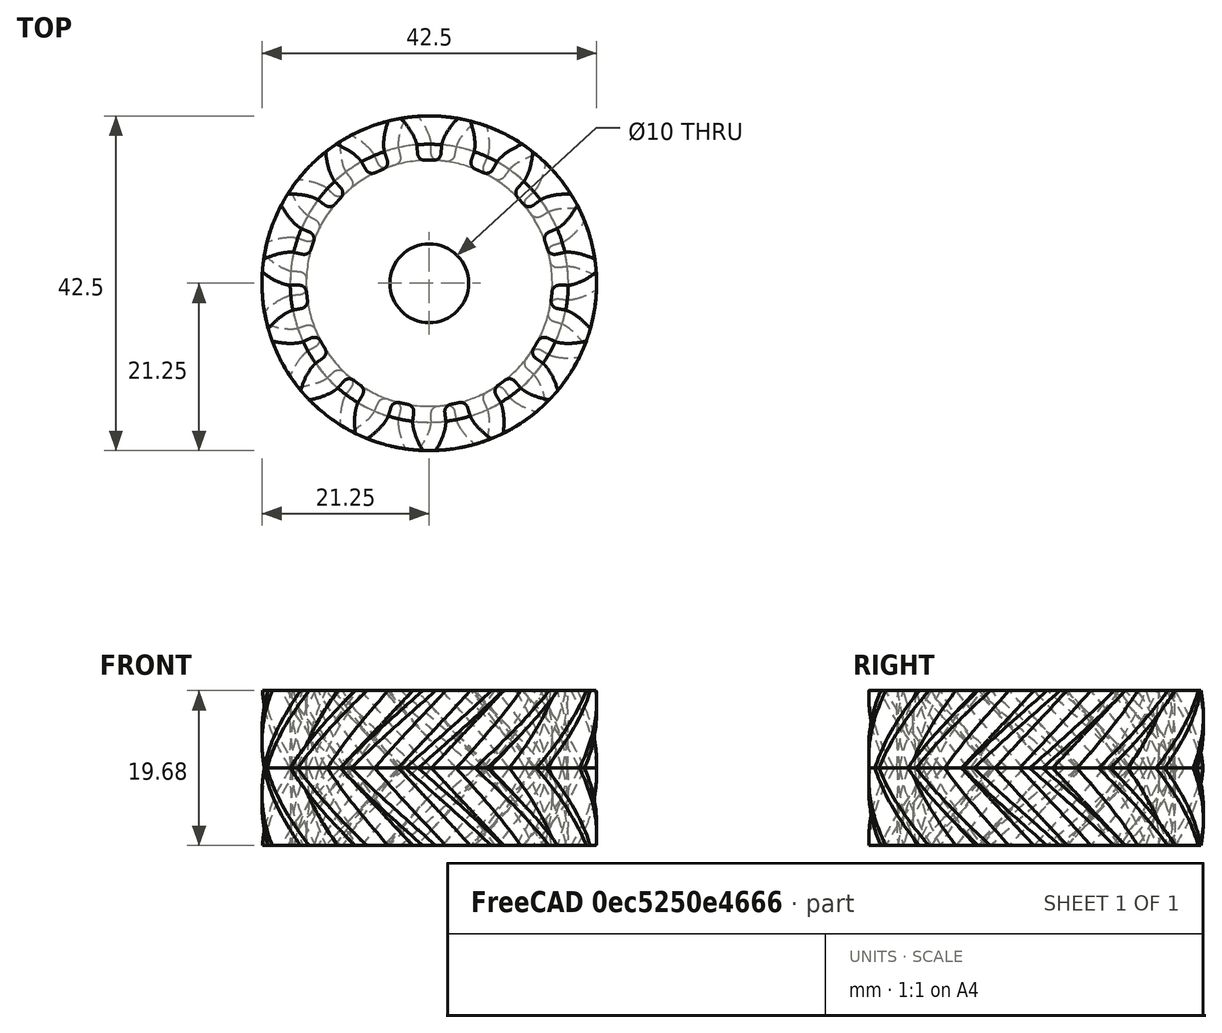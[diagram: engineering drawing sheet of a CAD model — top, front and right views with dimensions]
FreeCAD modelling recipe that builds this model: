
FCSTD DOCUMENT  (FreeCAD 0.20R29177 +426 (Git))
Label: Engranaje Chevron
License: All rights reserved
LicenseURL: http://en.wikipedia.org/wiki/All_rights_reserved
objects: Part::Part2DObjectPython×7, Part::Loft×1, Part::Mirroring×1, Part::MultiFuse×1, PartDesign::Body×1, Part::Cylinder×1, Part::Cut×1
note: 13 computed .brp shape members not serialized (recipe doc carries the construction recipe); baked Part::Feature solids carry a one-line shape summary decoded from their .brp

FEATURE [Part::Part2DObjectPython] InvoluteGear  # Draft 2D object (typed FeaturePython)
  ExternalGear = true
  HighPrecision = true
  Modules = 2.5
  NumberOfTeeth = 15
  PressureAngle = 20
FEATURE [Part::Part2DObjectPython] InvoluteGear001  # Draft 2D object (typed FeaturePython)
  ExternalGear = true
  HighPrecision = true
  Modules = 2.5
  NumberOfTeeth = 15
  Placement = pos=(0,0,1.64) rot=(0,0,1;0.087266rad)
  PressureAngle = 20
FEATURE [Part::Part2DObjectPython] InvoluteGear002  # Draft 2D object (typed FeaturePython)
  ExternalGear = true
  HighPrecision = true
  Modules = 2.5
  NumberOfTeeth = 15
  Placement = pos=(0,0,3.28) rot=(0,0,1;0.174533rad)
  PressureAngle = 20
FEATURE [Part::Part2DObjectPython] InvoluteGear003  # Draft 2D object (typed FeaturePython)
  ExternalGear = true
  HighPrecision = true
  Modules = 2.5
  NumberOfTeeth = 15
  Placement = pos=(0,0,4.92) rot=(0,0,1;0.261799rad)
  PressureAngle = 20
FEATURE [Part::Part2DObjectPython] InvoluteGear004  # Draft 2D object (typed FeaturePython)
  ExternalGear = true
  HighPrecision = true
  Modules = 2.5
  NumberOfTeeth = 15
  Placement = pos=(0,0,6.56) rot=(0,0,1;0.349066rad)
  PressureAngle = 20
FEATURE [Part::Part2DObjectPython] InvoluteGear005  # Draft 2D object (typed FeaturePython)
  ExternalGear = true
  HighPrecision = true
  Modules = 2.5
  NumberOfTeeth = 15
  Placement = pos=(0,0,8.2) rot=(0,0,1;0.436332rad)
  PressureAngle = 20
FEATURE [Part::Part2DObjectPython] InvoluteGear006  # Draft 2D object (typed FeaturePython)
  ExternalGear = true
  HighPrecision = true
  Modules = 2.5
  NumberOfTeeth = 15
  Placement = pos=(0,0,9.84) rot=(0,0,1;0.523599rad)
  PressureAngle = 20
FEATURE [Part::Loft] Loft
  Closed = false
  MaxDegree = 5
  Ruled = false
  Sections = -> [InvoluteGear,InvoluteGear001,InvoluteGear002,InvoluteGear003,InvoluteGear004,InvoluteGear005,InvoluteGear006]
  Solid = true
FEATURE [Part::Mirroring] Part__Mirroring  label="Loft (Mirror #1)"
  Base = (0,0,0)
  Normal = (0,0,1)
  Source = -> Loft
FEATURE [Part::MultiFuse] Fusion
  Shapes = -> [Part__Mirroring,Loft]
FEATURE [PartDesign::Body] Body
  Origin = -> Origin
FEATURE [Part::Cylinder] Cylinder  label="Cilindro"
  Angle = 360
  AttacherType = Attacher::AttachEngine3D
  FirstAngle = 0
  Height = 40
  Placement = pos=(0,0,-18) rot=(0,0,1;0rad)
  Radius = 5
  SecondAngle = 0
FEATURE [Part::Cut] Cut
  Base = -> Fusion
  Tool = -> Cylinder
